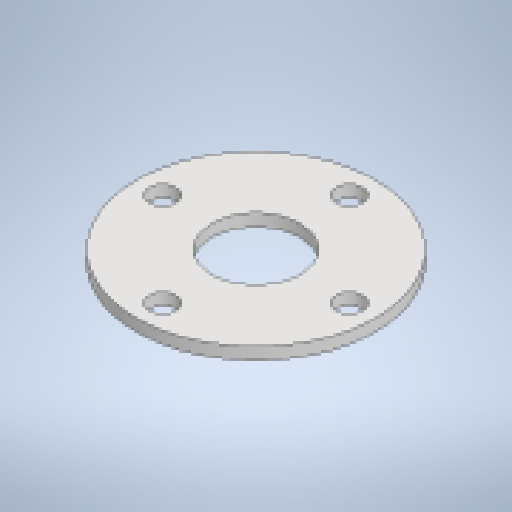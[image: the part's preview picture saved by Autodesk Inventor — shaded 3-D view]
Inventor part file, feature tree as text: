
AUTODESK INVENTOR PART (.ipt)
format: ipt  version: 2025.4 (Build 294407000, 407)  size: 192,000 bytes
history: native  units: mm
features: sketch x2, other x2, sheet_metal_op x1
ambient origin geometry x8: Origin, YZ Plane, XZ Plane, XY Plane, X Axis, Y Axis, Z Axis, Center Point
bodies: Body1 (feature_tree)
feature tree (5):
  sheet_metal_op  "Face2"
  sketch  "Sketch2"  dims[d33=360.0deg]
  other  "Plate2"
  sketch  "Sketch Circular Pattern1"  dims[d14=8.0mm]
  other  "Definition1"
